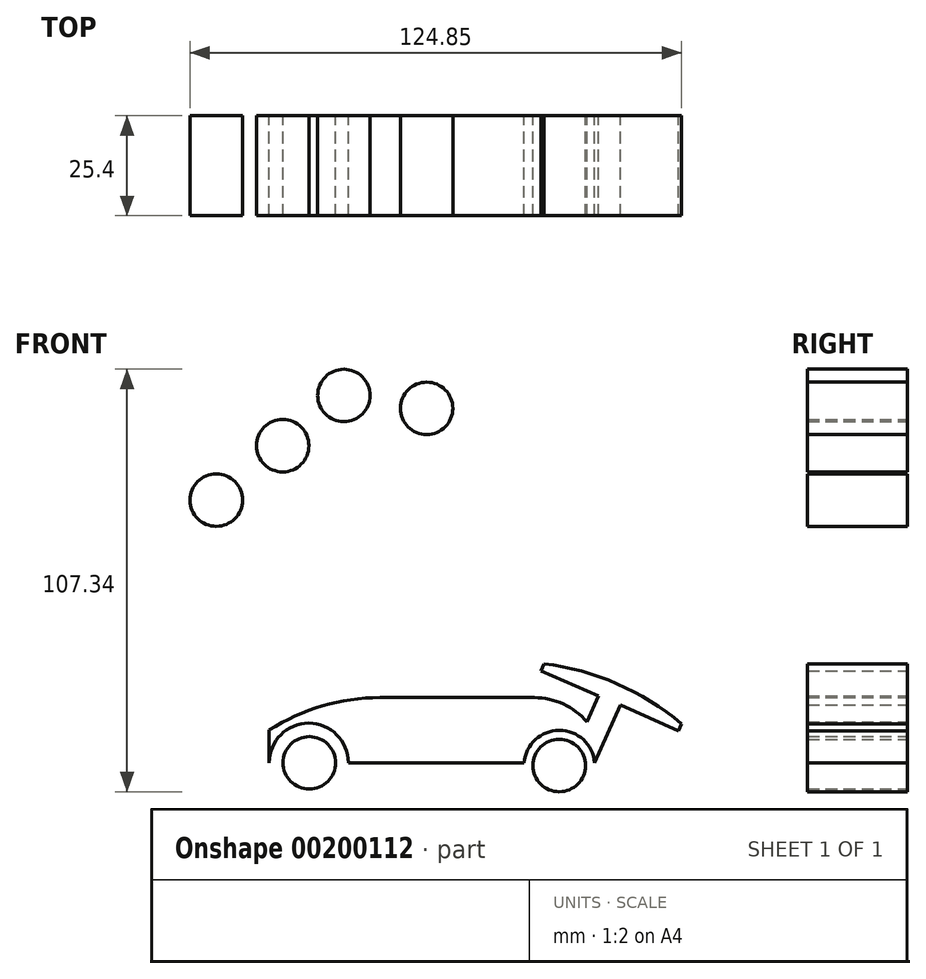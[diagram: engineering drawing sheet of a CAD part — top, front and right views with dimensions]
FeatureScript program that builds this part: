
annotation { "Feature Type Name" : "Feature", "Feature Type Description" : "" }
export const myFeature = defineFeature(function(context is Context, id is Id, definition is map)
    precondition{}
    {
        {
            var Q0;
            Q0=qCreatedBy(makeId("Front.planeOp"),FACE);
            var sketch = newSketch(context, id + "F0", { "sketchPlane" : qUnion([Q0])});
            skCircle(sketch, "E0", {"center": v(63.1, -32.3) * mm, "radius": 6.67 * mm});
            skCircle(sketch, "E1", {"center": v(79.96, -18.46) * mm, "radius": 6.67 * mm});
            skCircle(sketch, "E2", {"center": v(95.53, -5.7) * mm, "radius": 6.67 * mm});
            skPoint(sketch, "E3", {"position": v(93.05, 0.48) * mm});
            skCircle(sketch, "E4", {"center": v(116.53, -9) * mm, "radius": 6.67 * mm});
            skPoint(sketch, "E5", {"position": v(112.78, -3.49) * mm});
            skLineSegment(sketch, "E6.bottom", {"start": v(143.9, -82.47) * mm, "end": v(104.69, -82.47) * mm});
            skLineSegment(sketch, "E6.top", {"start": v(141.33, -99) * mm, "end": v(96.63, -99) * mm});
            skLineSegment(sketch, "E6.right", {"start": v(76.55, -90.74) * mm, "end": v(76.55, -99) * mm});
            skArc(sketch, "E7", {"start": v(159.17, -99) * mm, "mid": v(150.25, -90.76) * mm, "end": v(141.33, -99) * mm});
            skArc(sketch, "E8", {"start": v(76.55, -99) * mm, "mid": v(86.6, -88.96) * mm, "end": v(96.63, -99) * mm});
            skCircle(sketch, "E9", {"center": v(86.73, -99.05) * mm, "radius": 6.67 * mm});
            skCircle(sketch, "E10", {"center": v(150.22, -99.72) * mm, "radius": 6.67 * mm});
            skLineSegment(sketch, "E11", {"start": v(157.31, -88.7) * mm, "end": v(160.22, -82.02) * mm});
            skLineSegment(sketch, "E12", {"start": v(159.17, -99) * mm, "end": v(165.75, -84.36) * mm});
            skLineSegment(sketch, "E13", {"start": v(165.75, -84.36) * mm, "end": v(160.22, -82.02) * mm});
            skLineSegment(sketch, "E14", {"start": v(160.22, -82.02) * mm, "end": v(145.6, -75.66) * mm});
            skLineSegment(sketch, "E15", {"start": v(145.6, -75.66) * mm, "end": v(146.35, -73.87) * mm});
            skLineSegment(sketch, "E16", {"start": v(181.28, -89.1) * mm, "end": v(180.52, -90.9) * mm});
            skLineSegment(sketch, "E17", {"start": v(180.52, -90.9) * mm, "end": v(165.75, -84.36) * mm});
            skArc(sketch, "E18", {"start": v(104.69, -82.47) * mm, "mid": v(90.02, -84.58) * mm, "end": v(76.55, -90.74) * mm});
            skArc(sketch, "E19", {"start": v(181.28, -89.1) * mm, "mid": v(164.92, -78.96) * mm, "end": v(146.35, -73.87) * mm});
            skArc(sketch, "E20", {"start": v(157.31, -88.7) * mm, "mid": v(151.3, -84.1) * mm, "end": v(143.9, -82.47) * mm});
            skPoint(sketch, "E21", {"position": v(80.07, -99.05) * mm});
            skPoint(sketch, "E22", {"position": v(93.4, -99.05) * mm});
            skPoint(sketch, "E23", {"position": v(86.73, -92.38) * mm});
            skPoint(sketch, "E24", {"position": v(86.73, -105.71) * mm});
            skPoint(sketch, "E25", {"position": v(156.89, -99.71) * mm});
            skPoint(sketch, "E26", {"position": v(150.25, -93.05) * mm});
            skPoint(sketch, "E27", {"position": v(150.25, -106.38) * mm});
            skPoint(sketch, "E28", {"position": v(145.57, -94.95) * mm});
            skPoint(sketch, "E29", {"position": v(154.89, -94.96) * mm});
            skPoint(sketch, "E30", {"position": v(155, -104.37) * mm});
            skPoint(sketch, "E31", {"position": v(145.46, -104.38) * mm});
            skPoint(sketch, "E32", {"position": v(91.4, -103.81) * mm});
            skPoint(sketch, "E33", {"position": v(91.32, -94.2) * mm});
            skPoint(sketch, "E34", {"position": v(82.15, -94.2) * mm});
            skPoint(sketch, "E35", {"position": v(82.05, -103.8) * mm});
            skSolve(sketch);
        }
        {
            var Q0;
            Q0=makeQuery(id+"F0.imprint","IMPRINT",FACE,{"disambiguationData":[TD([[makeQuery(id+"F0.imprint","IMPRINT",EDGE,{"derivedFrom":sQuery(id+"F0.wireOp",EDGE,"E0")}),1.0]])]});
            var Q1;
            Q1=makeQuery(id+"F0.imprint","IMPRINT",FACE,{"disambiguationData":[TD([[makeQuery(id+"F0.imprint","IMPRINT",EDGE,{"derivedFrom":sQuery(id+"F0.wireOp",EDGE,"419a2961-f21f-443a-9de5-f49d51583728.0")}),-1.0]])]});
            extrude(context, id + "F1", {"entities" : qUnion([Q0, Q1]), "depth" : 25.4 * mm});
        }
        {
            var Q0;
            Q0 = qSketchRegion(id + "F0", true);
            extrude(context, id + "F2", {"entities" : qUnion([Q0]), "operationType" : NewBodyOperationType.ADD, "depth" : 25.4 * mm});
        }
    });
